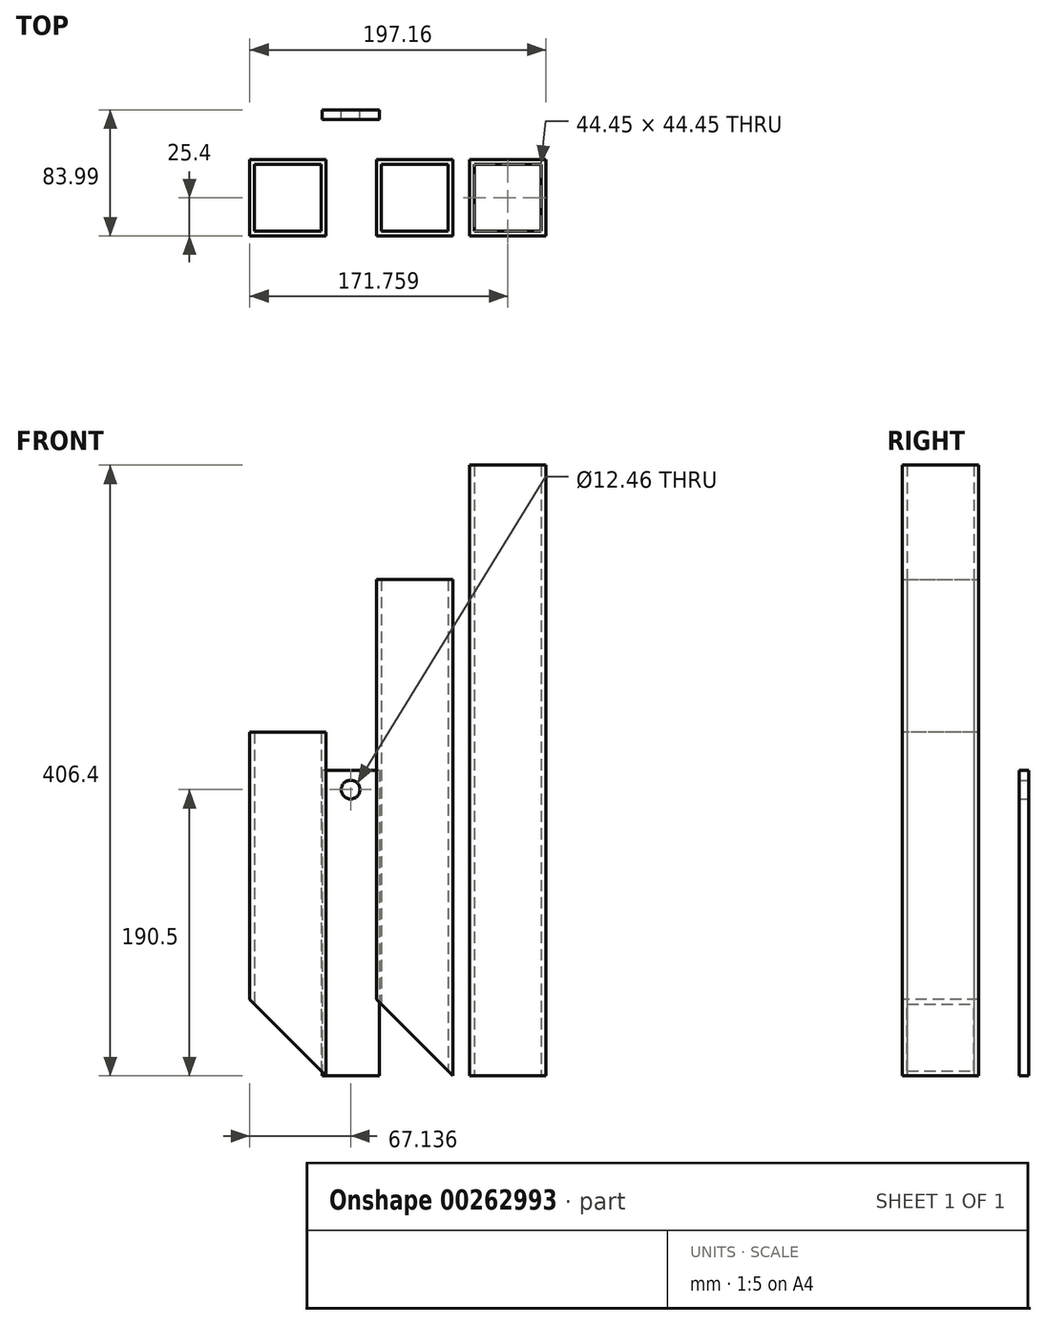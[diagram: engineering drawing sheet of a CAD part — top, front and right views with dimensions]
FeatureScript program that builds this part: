
annotation { "Feature Type Name" : "Feature", "Feature Type Description" : "" }
export const myFeature = defineFeature(function(context is Context, id is Id, definition is map)
    precondition{}
    {
        {
            var Q0;
            Q0=qCreatedBy(makeId("Top.planeOp"),FACE);
            var sketch = newSketch(context, id + "F0", { "sketchPlane" : qUnion([Q0])});
            skLineSegment(sketch, "E0.bottom", {"start": v(25.4, -25.4) * mm, "end": v(-25.4, -25.4) * mm});
            skLineSegment(sketch, "E0.top", {"start": v(25.4, 25.4) * mm, "end": v(-25.4, 25.4) * mm});
            skLineSegment(sketch, "E0.left", {"start": v(25.4, -25.4) * mm, "end": v(25.4, 25.4) * mm});
            skLineSegment(sketch, "E0.right", {"start": v(-25.4, -25.4) * mm, "end": v(-25.4, 25.4) * mm});
            skPoint(sketch, "E0.middle", {"position": v(0, 0) * mm});
            skLineSegment(sketch, "E1.bottom", {"start": v(22.22, -22.23) * mm, "end": v(-22.23, -22.23) * mm});
            skLineSegment(sketch, "E1.top", {"start": v(22.23, 22.23) * mm, "end": v(-22.22, 22.23) * mm});
            skLineSegment(sketch, "E1.left", {"start": v(22.23, -22.23) * mm, "end": v(22.23, 22.23) * mm});
            skLineSegment(sketch, "E1.right", {"start": v(-22.23, -22.23) * mm, "end": v(-22.23, 22.23) * mm});
            skLineSegment(sketch, "E2.bottom", {"start": v(-109.82, 25.4) * mm, "end": v(-59.02, 25.4) * mm});
            skLineSegment(sketch, "E2.top", {"start": v(-109.82, -25.4) * mm, "end": v(-59.02, -25.4) * mm});
            skLineSegment(sketch, "E2.left", {"start": v(-109.82, 25.4) * mm, "end": v(-109.82, -25.4) * mm});
            skLineSegment(sketch, "E2.right", {"start": v(-59.02, 25.4) * mm, "end": v(-59.02, -25.4) * mm});
            skPoint(sketch, "E2.middle", {"position": v(-84.42, 0) * mm});
            skLineSegment(sketch, "E3.bottom", {"start": v(-106.65, 22.23) * mm, "end": v(-62.2, 22.23) * mm});
            skLineSegment(sketch, "E3.top", {"start": v(-106.65, -22.22) * mm, "end": v(-62.2, -22.22) * mm});
            skLineSegment(sketch, "E3.left", {"start": v(-106.65, 22.23) * mm, "end": v(-106.65, -22.23) * mm});
            skLineSegment(sketch, "E3.right", {"start": v(-62.2, 22.23) * mm, "end": v(-62.2, -22.22) * mm});
            skLineSegment(sketch, "E4.bottom", {"start": v(87.34, 25.4) * mm, "end": v(36.54, 25.4) * mm});
            skLineSegment(sketch, "E4.top", {"start": v(87.34, -25.4) * mm, "end": v(36.54, -25.4) * mm});
            skLineSegment(sketch, "E4.left", {"start": v(87.34, 25.4) * mm, "end": v(87.34, -25.4) * mm});
            skLineSegment(sketch, "E4.right", {"start": v(36.54, 25.4) * mm, "end": v(36.54, -25.4) * mm});
            skPoint(sketch, "E4.middle", {"position": v(61.94, 0) * mm});
            skLineSegment(sketch, "E5.bottom", {"start": v(84.16, 22.23) * mm, "end": v(39.71, 22.23) * mm});
            skLineSegment(sketch, "E5.top", {"start": v(84.16, -22.23) * mm, "end": v(39.71, -22.23) * mm});
            skLineSegment(sketch, "E5.left", {"start": v(84.16, 22.22) * mm, "end": v(84.16, -22.22) * mm});
            skLineSegment(sketch, "E5.right", {"start": v(39.71, 22.22) * mm, "end": v(39.71, -22.22) * mm});
            skSolve(sketch);
        }
        {
            var Q0;
            Q0=makeQuery(id+"F0.imprint","IMPRINT",FACE,{"disambiguationData":[TD([[makeQuery(id+"F0.imprint","IMPRINT",EDGE,{"derivedFrom":sQuery(id+"F0.wireOp",EDGE,"E2.bottom")}),-1.0]])]});
            extrude(context, id + "F1", {"entities" : qUnion([Q0]), "depth" : 228.6 * mm});
        }
        {
            var Q0;
            Q0=makeQuery(id+"F0.imprint","IMPRINT",FACE,{"disambiguationData":[TD([[makeQuery(id+"F0.imprint","IMPRINT",EDGE,{"derivedFrom":sQuery(id+"F0.wireOp",EDGE,"E0.bottom")}),-1.0]])]});
            extrude(context, id + "F2", {"entities" : qUnion([Q0]), "depth" : 330.2 * mm});
        }
        {
            var Q0;
            Q0=makeQuery(id+"F0.imprint","IMPRINT",FACE,{"disambiguationData":[TD([[makeQuery(id+"F0.imprint","IMPRINT",EDGE,{"derivedFrom":sQuery(id+"F0.wireOp",EDGE,"E4.bottom")}),1.0]])]});
            extrude(context, id + "F3", {"entities" : qUnion([Q0]), "depth" : 406.4 * mm});
        }
        {
            var Q0;
            Q0=makeQuery(id+"F1.opExtrude","SWEPT_FACE",FACE,{"disambiguationData":[OSD([sQuery(id+"F0.wireOp",EDGE,"E2.top")])]});
            var sketch = newSketch(context, id + "F4", { "sketchPlane" : qUnion([Q0])});
            skLineSegment(sketch, "E6", {"start": v(-59.02, 0) * mm, "end": v(-109.82, 50.8) * mm});
            skLineSegment(sketch, "E7", {"start": v(-109.82, 50.8) * mm, "end": v(-109.82, 0) * mm});
            skLineSegment(sketch, "E8", {"start": v(-109.82, 0) * mm, "end": v(-59.02, 0) * mm});
            skSolve(sketch);
        }
        {
            var Q0;
            Q0=makeQuery(id+"F4.imprint","IMPRINT",FACE,{"disambiguationData":[TD([[makeQuery(id+"F4.imprint","IMPRINT",EDGE,{"derivedFrom":sQuery(id+"F4.wireOp",EDGE,"E6")}),1.0]])]});
            extrude(context, id + "F5", {"entities" : qUnion([Q0]), "operationType" : NewBodyOperationType.REMOVE, "oppositeDirection" : true, "depth" : 50.8 * mm});
        }
        {
            var Q0;
            Q0=makeQuery(id+"F2.opExtrude","SWEPT_FACE",FACE,{"disambiguationData":[OSD([sQuery(id+"F0.wireOp",EDGE,"E0.bottom")])]});
            var sketch = newSketch(context, id + "F6", { "sketchPlane" : qUnion([Q0])});
            skLineSegment(sketch, "E9", {"start": v(25.4, 0) * mm, "end": v(-25.4, 50.8) * mm});
            skLineSegment(sketch, "E10", {"start": v(-25.4, 50.8) * mm, "end": v(-25.4, 0) * mm});
            skLineSegment(sketch, "E11", {"start": v(-25.4, 0) * mm, "end": v(25.4, 0) * mm});
            skSolve(sketch);
        }
        {
            var Q0;
            Q0=makeQuery(id+"F6.imprint","IMPRINT",FACE,{"disambiguationData":[TD([[makeQuery(id+"F6.imprint","IMPRINT",EDGE,{"derivedFrom":sQuery(id+"F6.wireOp",EDGE,"E9")}),1.0]])]});
            extrude(context, id + "F7", {"entities" : qUnion([Q0]), "operationType" : NewBodyOperationType.REMOVE, "oppositeDirection" : true, "depth" : 50.8 * mm});
        }
        {
            var Q0;
            Q0=qCreatedBy(makeId("Top.planeOp"),FACE);
            var sketch = newSketch(context, id + "F8", { "sketchPlane" : qUnion([Q0])});
            skLineSegment(sketch, "E12.bottom", {"start": v(-23.63, 52.24) * mm, "end": v(-61.73, 52.24) * mm});
            skLineSegment(sketch, "E12.top", {"start": v(-23.63, 58.59) * mm, "end": v(-61.73, 58.59) * mm});
            skLineSegment(sketch, "E12.left", {"start": v(-23.63, 52.24) * mm, "end": v(-23.63, 58.59) * mm});
            skLineSegment(sketch, "E12.right", {"start": v(-61.73, 52.24) * mm, "end": v(-61.73, 58.59) * mm});
            skPoint(sketch, "E12.middle", {"position": v(-42.68, 55.41) * mm});
            skSolve(sketch);
        }
        {
            var Q0;
            Q0=makeQuery(id+"F8.imprint","IMPRINT",FACE,{"disambiguationData":[TD([[makeQuery(id+"F8.imprint","IMPRINT",EDGE,{"derivedFrom":sQuery(id+"F8.wireOp",EDGE,"E12.bottom")}),-1.0]])]});
            extrude(context, id + "F9", {"entities" : qUnion([Q0]), "depth" : 203.2 * mm});
        }
        {
            var Q0;
            Q0=makeQuery(id+"F9.opExtrude","SWEPT_FACE",FACE,{"disambiguationData":[OSD([sQuery(id+"F8.wireOp",EDGE,"E12.top")])]});
            var sketch = newSketch(context, id + "F10", { "sketchPlane" : qUnion([Q0])});
            skCircle(sketch, "E13", {"center": v(42.68, 190.5) * mm, "radius": 6.23 * mm});
            skSolve(sketch);
        }
        {
            var Q0;
            Q0=makeQuery(id+"F10.imprint","IMPRINT",FACE,{"disambiguationData":[TD([[makeQuery(id+"F10.imprint","IMPRINT",EDGE,{"derivedFrom":sQuery(id+"F10.wireOp",EDGE,"E13")}),1.0]])]});
            extrude(context, id + "F11", {"entities" : qUnion([Q0]), "operationType" : NewBodyOperationType.REMOVE, "oppositeDirection" : true, "depth" : 25.4 * mm});
        }
    });
